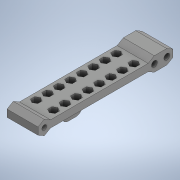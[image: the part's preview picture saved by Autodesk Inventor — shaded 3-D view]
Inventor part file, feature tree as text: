
AUTODESK INVENTOR PART (.ipt)
format: ipt  version: 2020 (Build 240168000, 168)  size: 555,008 bytes
history: native  units: in
note: dims shown in document units (in); Inventor stores cm internally (conversion verified against a paired STEP export)
features: sketch x7, extrude x6, projected_geometry x4, plane x2, mirror x1, fillet x1
ambient origin geometry x8: Origin, YZ Plane, XZ Plane, XY Plane, X Axis, Y Axis, Z Axis, Center Point
bodies: Solid1 (feature_tree)
feature tree (21):
  extrude  "Extrusion1"  Depth=3.4256in
  plane  "Work Plane1"
  extrude  "Extrusion2"  Depth=0.7874in
  sketch  "Sketch4"  dims[d4=0.0in d5=0.0906in]
  extrude  "Extrusion4"  Depth=0.0906in
  plane  "Work Plane2"
  extrude  "Extrusion6"  Depth=3.1106in
  mirror  "Mirror2"
  extrude  "Extrusion7"  Depth=0.315in
  extrude  "Extrusion8"  Depth=0.2362in
  fillet  "Fillet1"  [1 undecoded]
  sketch  "Sketch1"  dims[d0=0.1818in d1=3.4256in]
  sketch  "Sketch2"  dims[d2=0.122in d3=0.7874in]
  sketch  "Sketch5"  dims[d6=0.7874in d7=0.0in d28=3.1106in]
  sketch  "Sketch7"  dims[d29=0.315in d31=0.315in]
  projected_geometry  "Projected Loop7"
  projected_geometry  "Projected Loop8"
  sketch  "Sketch8"  dims[d33=0.1476in d34=0.2362in d35=0.0in]
  projected_geometry  "Projected Loop9"
  sketch  "Sketch10"  dims[d38=0.315in d39=0.2756in d40=-0.3092in d41=0.0787in d42=0.0787in d43=0.0787in d44=3.1496in d46=0.2913in d47=0.3937in d49=0.3937in d51=3.1496in d53=0.2913in d54=0.3937in d56=0.3937in d58=0.0in d59=0.0in d60=1.0994in d61=0.1378in d63=1.1811in d64=0.1575in d65=0.0in d66=0.126in d67=0.1575in d69=2.4807in]
  projected_geometry  "Projected Loop10"
note: 1 required parameter value undecoded (feature->parameter linkage not recoverable at this tier; creation-order binding heuristic only, values carry confidence <= 0.55)
